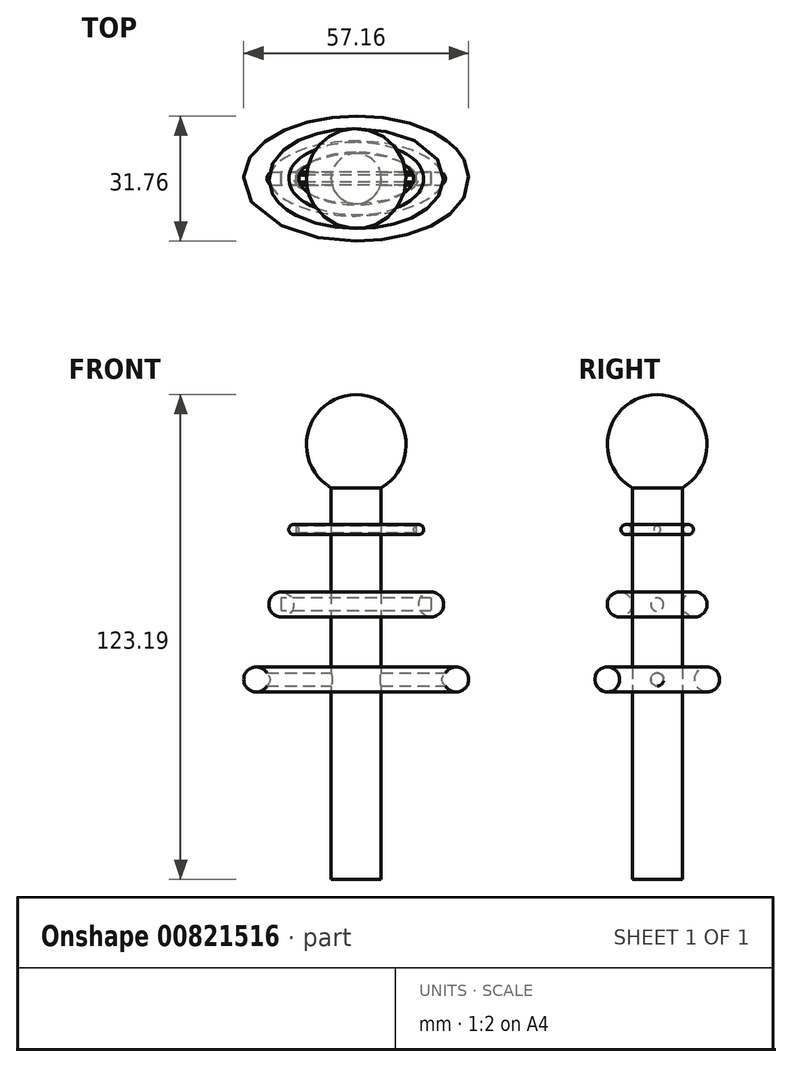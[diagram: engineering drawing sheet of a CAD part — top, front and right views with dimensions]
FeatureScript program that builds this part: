
annotation { "Feature Type Name" : "Feature", "Feature Type Description" : "" }
export const myFeature = defineFeature(function(context is Context, id is Id, definition is map)
    precondition{}
    {
        {
            var Q0;
            Q0=qCreatedBy(makeId("Top.planeOp"),FACE);
            var sketch = newSketch(context, id + "F0", { "sketchPlane" : qUnion([Q0])});
            skCircle(sketch, "E0", {"center": v(0, 0) * mm, "radius": 6.35 * mm});
            skSolve(sketch);
        }
        {
            var Q0;
            Q0 = qSketchRegion(id + "F0", true);
            extrude(context, id + "F1", {"entities" : qUnion([Q0]), "endBound" : BoundingType.SYMMETRIC, "depth" : 101.6 * mm, "offsetDistance" : 25.4 * mm});
        }
        {
            var Q0;
            Q0=qCreatedBy(makeId("Top.planeOp"),FACE);
            var sketch = newSketch(context, id + "F2", { "sketchPlane" : qUnion([Q0])});
            skEllipse(sketch, "E1", {"center": v(0, 0) * mm, "majorRadius": 25.4 * mm, "minorRadius": 12.7 * mm, "majorAxis": v(-1, 0)});
            skSolve(sketch);
        }
        {
            var Q0;
            Q0=qCreatedBy(makeId("Right.planeOp"),FACE);
            var sketch = newSketch(context, id + "F3", { "sketchPlane" : qUnion([Q0])});
            skCircle(sketch, "E2", {"center": v(12.7, 0) * mm, "radius": 3.18 * mm});
            skSolve(sketch);
        }
        {
            var Q0;
            Q0 = qSketchRegion(id + "F3", true);
            var Q1;
            Q1 = qConstructionFilter(qBodyType(qCreatedBy(id + "F2" ,EDGE), BodyType.WIRE), ConstructionObject.NO);
            sweep(context, id + "F4", {"profiles" : qUnion([Q0]), "path" : qUnion([Q1])});
        }
        {
            var Q0;
            Q0=qCreatedBy(makeId("Top.planeOp"),FACE);
            cPlane(context, id + "F5", {"entities" : qUnion([Q0]), "cplaneType" : CPlaneType.OFFSET, "offset" : 19.05 * mm, "width" : 152.4 * mm, "height" : 152.4 * mm});
        }
        {
            var Q0;
            Q0=qCreatedBy(id+"F5.planeOp",FACE);
            var sketch = newSketch(context, id + "F6", { "sketchPlane" : qUnion([Q0])});
            skEllipse(sketch, "E3.0", {"center": v(0, 0) * mm, "majorRadius": 19.05 * mm, "minorRadius": 9.53 * mm, "majorAxis": v(-1, 0)});
            skSolve(sketch);
        }
        {
            var Q0;
            Q0=qCreatedBy(makeId("Right.planeOp"),FACE);
            var sketch = newSketch(context, id + "F7", { "sketchPlane" : qUnion([Q0])});
            skCircle(sketch, "E4", {"center": v(9.53, 19.07) * mm, "radius": 3.17 * mm});
            skSolve(sketch);
        }
        {
            var Q0;
            Q0=makeQuery(id+"F7.imprint","IMPRINT",FACE,{"disambiguationData":[TD([[makeQuery(id+"F7.imprint","IMPRINT",EDGE,{"derivedFrom":sQuery(id+"F7.wireOp",EDGE,"E4")}),1.0]])]});
            var Q1;
            Q1=sQuery(id+"F6.wireOp",EDGE,"E3.0");
            sweep(context, id + "F8", {"profiles" : qUnion([Q0]), "path" : qUnion([Q1])});
        }
        {
            var Q0;
            Q0=qCreatedBy(id+"F5.planeOp",FACE);
            cPlane(context, id + "F9", {"entities" : qUnion([Q0]), "cplaneType" : CPlaneType.OFFSET, "offset" : 19.05 * mm, "width" : 152.4 * mm, "height" : 152.4 * mm});
        }
        {
            var Q0;
            Q0=qCreatedBy(id+"F9.planeOp",FACE);
            var sketch = newSketch(context, id + "F10", { "sketchPlane" : qUnion([Q0])});
            skEllipse(sketch, "E5.0", {"center": v(0, 0) * mm, "majorRadius": 15.88 * mm, "minorRadius": 7.94 * mm, "majorAxis": v(-1, 0)});
            skSolve(sketch);
        }
        {
            var Q0;
            Q0=qCreatedBy(makeId("Right.planeOp"),FACE);
            var sketch = newSketch(context, id + "F11", { "sketchPlane" : qUnion([Q0])});
            skCircle(sketch, "E6", {"center": v(7.94, 38.1) * mm, "radius": 1.27 * mm});
            skSolve(sketch);
        }
        {
            var Q0;
            Q0=makeQuery(id+"F11.imprint","IMPRINT",FACE,{"disambiguationData":[TD([[makeQuery(id+"F11.imprint","IMPRINT",EDGE,{"derivedFrom":sQuery(id+"F11.wireOp",EDGE,"E6")}),1.0]])]});
            var Q1;
            Q1=sQuery(id+"F10.wireOp",EDGE,"E5.0");
            sweep(context, id + "F12", {"profiles" : qUnion([Q0]), "path" : qUnion([Q1])});
        }
        {
            var Q0;
            Q0=qCreatedBy(makeId("Top.planeOp"),FACE);
            var sketch = newSketch(context, id + "F13", { "sketchPlane" : qUnion([Q0])});
            skLineSegment(sketch, "E7", {"start": v(0, 0) * mm, "end": v(-25.4, 0) * mm});
            skLineSegment(sketch, "E8", {"start": v(0, 0) * mm, "end": v(25.4, 0) * mm});
            skLineSegment(sketch, "E9", {"start": v(-25.4, 0) * mm, "end": v(-25.4, 1.65) * mm});
            skLineSegment(sketch, "E10", {"start": v(-25.4, 1.65) * mm, "end": v(25.4, 1.65) * mm});
            skLineSegment(sketch, "E11", {"start": v(25.4, 1.65) * mm, "end": v(25.4, 0) * mm});
            skSolve(sketch);
        }
        {
            var Q0;
            Q0 = qSketchRegion(id + "F13", true);
            var Q1;
            Q1=sQuery(id+"F13.wireOp",EDGE,"E7");
            revolve(context, id + "F14", {"operationType" : NewBodyOperationType.ADD, "surfaceOperationType" : NewSurfaceOperationType.NEW, "entities" : qUnion([Q0]), "axis" : qUnion([Q1]), "revolveType" : RevolveType.FULL});
        }
        {
            var Q0;
            Q0=qCreatedBy(id+"F5.planeOp",FACE);
            var sketch = newSketch(context, id + "F15", { "sketchPlane" : qUnion([Q0])});
            skPoint(sketch, "E12.orphan", {"position": v(0, 0) * mm});
            skLineSegment(sketch, "E13", {"start": v(0, 0) * mm, "end": v(0, 19.14) * mm, "construction": true});
            skLineSegment(sketch, "E14", {"start": v(-19.05, 0) * mm, "end": v(19.05, 0) * mm});
            skLineSegment(sketch, "E15", {"start": v(-19.05, 0) * mm, "end": v(-19.05, 1.65) * mm});
            skLineSegment(sketch, "E16", {"start": v(-19.05, 1.65) * mm, "end": v(19.05, 1.65) * mm});
            skLineSegment(sketch, "E17", {"start": v(19.05, 1.65) * mm, "end": v(19.05, 0) * mm});
            skPoint(sketch, "E18.0.end.orphan", {"position": v(25.4, 0) * mm});
            skSolve(sketch);
        }
        {
            var Q0;
            Q0=makeQuery(id+"F15.imprint","IMPRINT",FACE,{"disambiguationData":[TD([[makeQuery(id+"F15.imprint","IMPRINT",EDGE,{"derivedFrom":sQuery(id+"F15.wireOp",EDGE,"E14")}),1.0]])]});
            var Q1;
            Q1=sQuery(id+"F15.wireOp",EDGE,"E14");
            revolve(context, id + "F16", {"surfaceOperationType" : NewSurfaceOperationType.NEW, "entities" : qUnion([Q0]), "axis" : qUnion([Q1]), "revolveType" : RevolveType.FULL});
        }
        {
            var Q0;
            Q0=qCreatedBy(id+"F9.planeOp",FACE);
            var sketch = newSketch(context, id + "F17", { "sketchPlane" : qUnion([Q0])});
            skLineSegment(sketch, "E19", {"start": v(-15.24, 0) * mm, "end": v(15.24, 0) * mm});
            skLineSegment(sketch, "E20", {"start": v(15.24, 0) * mm, "end": v(15.24, 0.89) * mm});
            skLineSegment(sketch, "E21", {"start": v(15.24, 0.89) * mm, "end": v(-15.24, 0.89) * mm});
            skLineSegment(sketch, "E22", {"start": v(-15.24, 0.89) * mm, "end": v(-15.24, 0) * mm});
            skLineSegment(sketch, "E23", {"start": v(0, 0) * mm, "end": v(0, 13.8) * mm});
            skSolve(sketch);
        }
        {
            var Q0;
            Q0 = qSketchRegion(id + "F17", true);
            var Q1;
            Q1=sQuery(id+"F17.wireOp",EDGE,"E19");
            revolve(context, id + "F18", {"surfaceOperationType" : NewSurfaceOperationType.NEW, "entities" : qUnion([Q0]), "axis" : qUnion([Q1]), "revolveType" : RevolveType.FULL});
        }
        {
            var Q0;
            Q0=qCreatedBy(makeId("Front.planeOp"),FACE);
            var sketch = newSketch(context, id + "F19", { "sketchPlane" : qUnion([Q0])});
            skArc(sketch, "E24", {"start": v(0, 72.4) * mm, "mid": v(-12.68, 59.69) * mm, "end": v(0, 47) * mm});
            skPoint(sketch, "E24.first.point", {"position": v(0, 47) * mm});
            skPoint(sketch, "E24.second.point", {"position": v(0, 72.4) * mm});
            skPoint(sketch, "E24.third.point", {"position": v(0, 72.4) * mm});
            skLineSegment(sketch, "E25", {"start": v(0, 72.4) * mm, "end": v(0, 47) * mm});
            skSolve(sketch);
        }
        {
            var Q0;
            Q0 = qSketchRegion(id + "F19", true);
            var Q1;
            Q1=sQuery(id+"F19.wireOp",EDGE,"E25");
            revolve(context, id + "F20", {"operationType" : NewBodyOperationType.ADD, "surfaceOperationType" : NewSurfaceOperationType.NEW, "entities" : qUnion([Q0]), "axis" : qUnion([Q1]), "revolveType" : RevolveType.FULL});
        }
    });
